# Revit family: MG GOBI TDS
name_source: partatom
category: Aparatos sanitarios
revit_build: Autodesk Revit 2016 (Build: 20150220_1215(x64)
units: mm (PartAtom-declared; Revit-internal decimal feet)

## family parameters
Compartido = No
Corte con vacíos al cargar = No
Cota de conector redondo = Diámetro de uso
Número OmniClass = 23.45.00.00
Punto de cálculo de habitación = No
Se basa en plano de trabajo = No
Siempre vertical = Sí
Tipo de pieza = Normal
Título OmniClass = Sanitary, Laundry, and Cleaning Equipment

## types (1)
- MG GOBY TDS
    Ceramic = High Gloss Ceramic
    Certification = http://www.helvex.com.mx
    Comentarios de tipo = Urinals
    Conexión de residuos = Sí
    Descripción = Negev TDS Dry Urinal
    Documentation = http://www.helvex.com.mx
    Fabricante = Helvex
    Features = Perfect Seal That Keeps Odor Away, Water Not Required, Easy Installation
    High Density Polypropylene = Polypropylene
    Inlet Threads = Flush: 1.5" (38 mm)
    Instructive = http://www.helvex.com.mx
    Modelo = MG0-E
    Teflon Cartridge Base = Teflon
    Total Height = 25"
    Total Length = 16"
    Total Width = 11"
    URL = http://www.helvex.com.mx

## geometry (parser evidence)
native form markers: Sweep x3
no freeform markers — native parametric forms only
